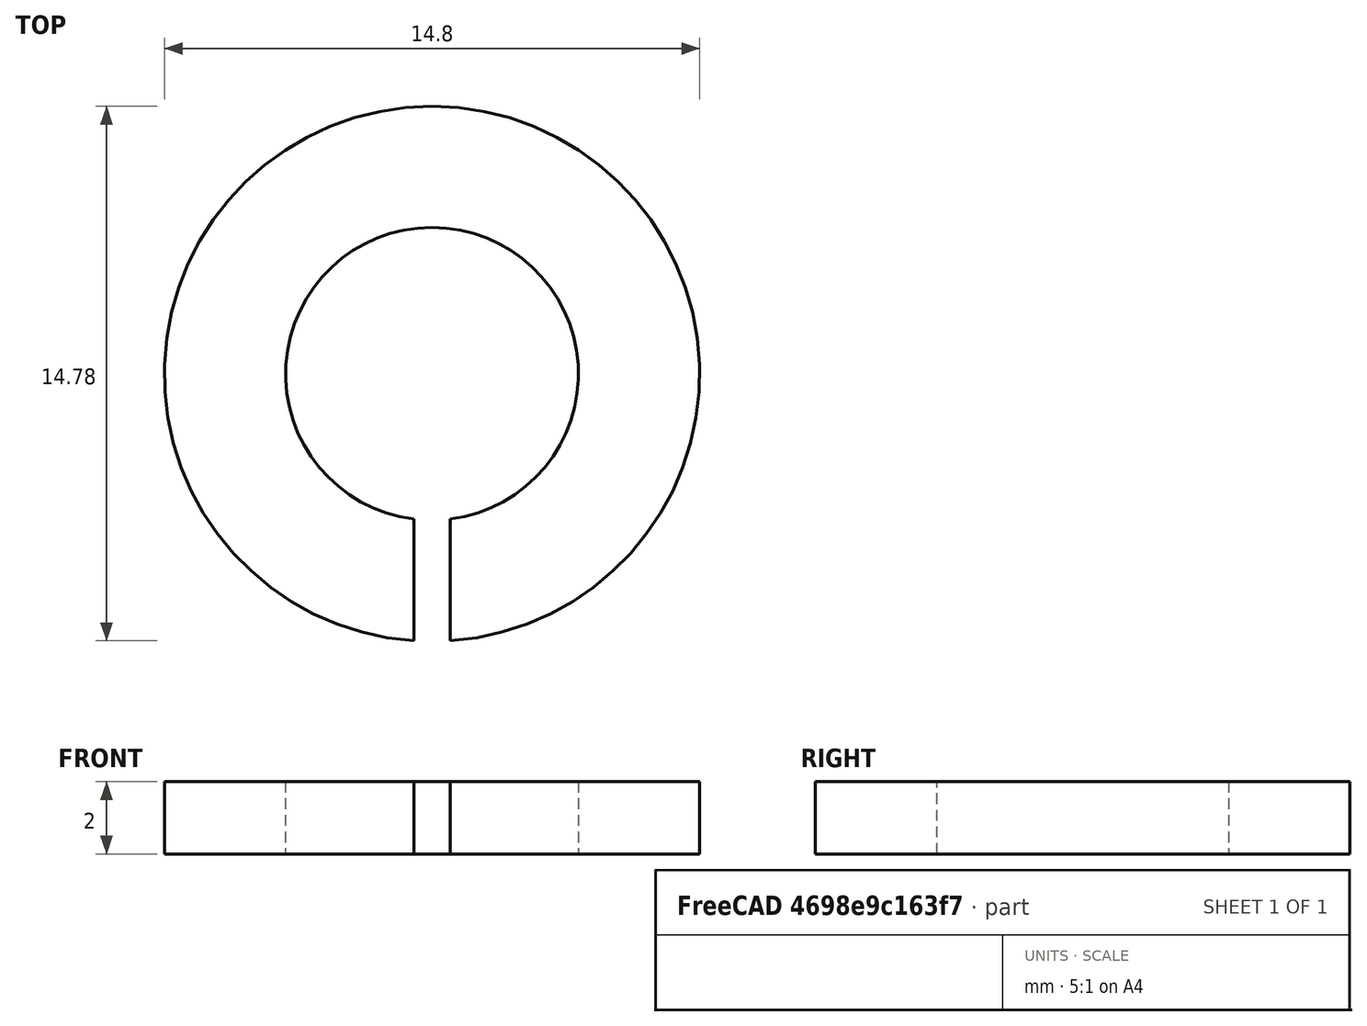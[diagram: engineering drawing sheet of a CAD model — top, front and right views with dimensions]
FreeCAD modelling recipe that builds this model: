
FCSTD DOCUMENT  (FreeCAD 0.15R4651 (Git))
Label: Federring_DIN127-A8
License: All rights reserved
LicenseURL: http://de.wikipedia.org/wiki/Alle_Rechte_vorbehalten
objects: Sketcher::SketchObject×1, PartDesign::Pad×1
note: 3 computed .brp shape members not serialized (recipe doc carries the construction recipe); baked Part::Feature solids carry a one-line shape summary decoded from their .brp

FEATURE [Sketcher::SketchObject] Sketch
  sketch-geometry (4):
    g0: ArcOfCircle CenterX=0 CenterY=0 CenterZ=0 NormalX=0 NormalY=0 NormalZ=1 Radius=4.05 StartAngle=4.83616 EndAngle=10.8718
    g1: ArcOfCircle CenterX=0 CenterY=0 CenterZ=0 NormalX=0 NormalY=0 NormalZ=1 Radius=7.4 StartAngle=4.78001 EndAngle=10.928
    g2: LineSegment StartX=0.5 StartY=-4.01902 StartZ=0 EndX=0.5 EndY=-7.38309 EndZ=0
    g3: LineSegment StartX=-0.5 StartY=-7.38309 StartZ=0 EndX=-0.5 EndY=-4.01902 EndZ=0
  constraints (12):
    c: Coincident(g0,g-1)
    c: Coincident(g1,g-1)
    c: Vertical(g2)
    c: Vertical(g3)
    c: Coincident(g0,g2)
    c: Coincident(g0,g3)
    c: Coincident(g1,g2)
    c: Coincident(g1,g3)
    c: Symmetric(g1,g1,g-2)
    c: Radius(g0) = 4.05
    c: Radius(g1) = 7.4
    c: DistanceX(g1,g1) = -1
FEATURE [PartDesign::Pad] Pad  label="Federring DIN 127-A 8 #"
  Length = 2
  Length2 = 100
  Midplane = true
  Sketch = -> Sketch
  Type = 0
